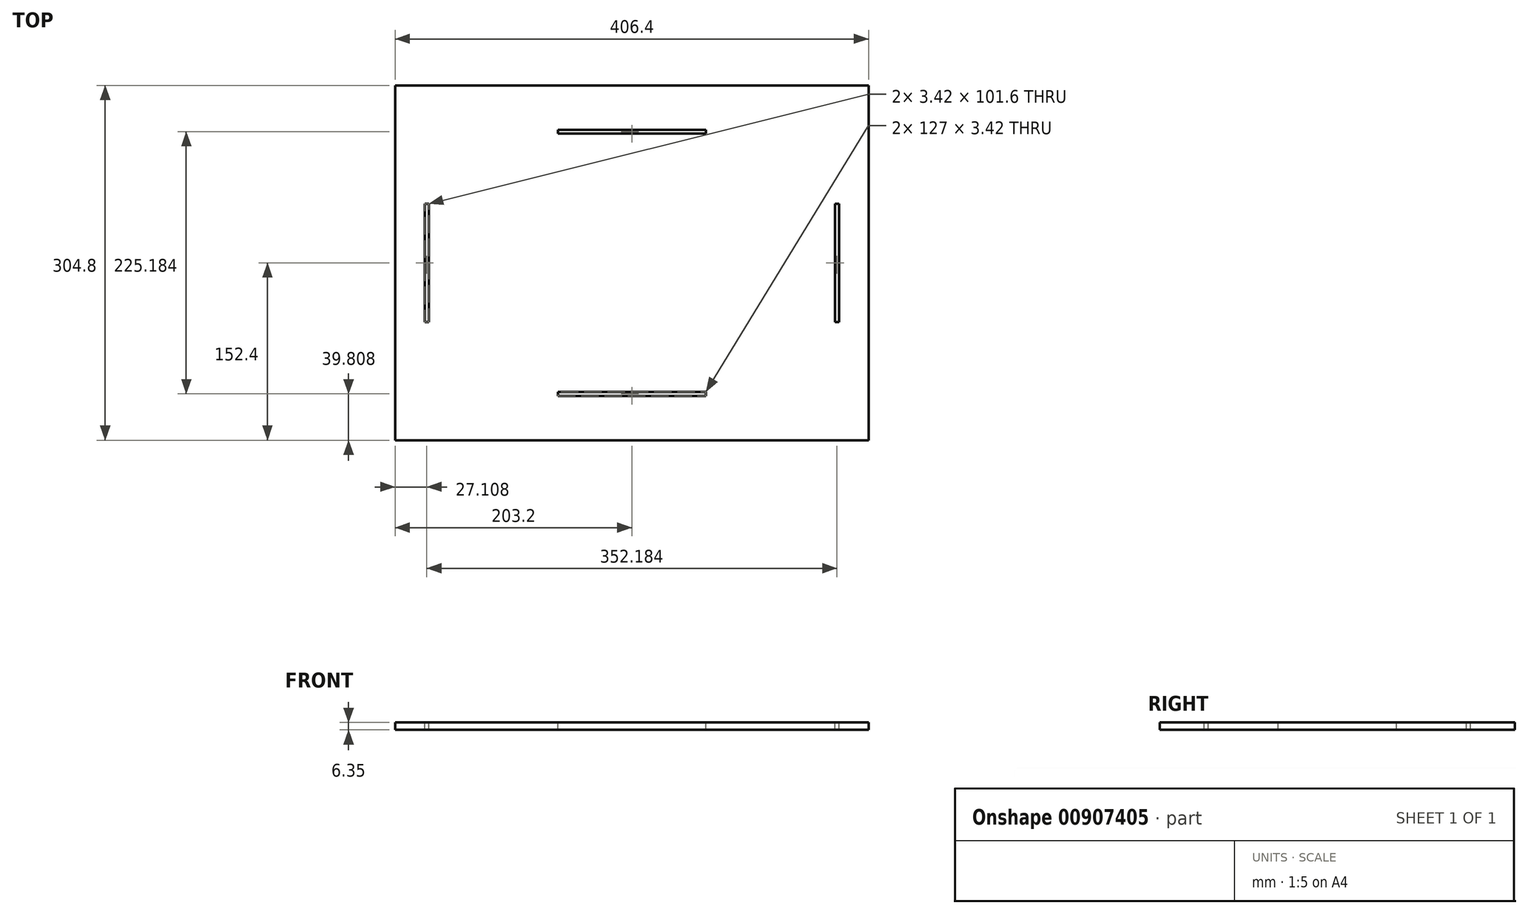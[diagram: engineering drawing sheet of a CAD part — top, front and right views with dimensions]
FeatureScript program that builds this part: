
annotation { "Feature Type Name" : "Feature", "Feature Type Description" : "" }
export const myFeature = defineFeature(function(context is Context, id is Id, definition is map)
    precondition{}
    {
        {
            var Q0;
            Q0=qCreatedBy(makeId("Top.planeOp"),FACE);
            var sketch = newSketch(context, id + "F0", { "sketchPlane" : qUnion([Q0])});
            skLineSegment(sketch, "E0.bottom", {"start": v(-203.2, 152.4) * mm, "end": v(203.2, 152.4) * mm});
            skLineSegment(sketch, "E0.top", {"start": v(-203.2, -152.4) * mm, "end": v(203.2, -152.4) * mm});
            skLineSegment(sketch, "E0.left", {"start": v(-203.2, 152.4) * mm, "end": v(-203.2, -152.4) * mm});
            skLineSegment(sketch, "E0.right", {"start": v(203.2, 152.4) * mm, "end": v(203.2, -152.4) * mm});
            skLineSegment(sketch, "E1.bottom", {"start": v(-177.8, 50.8) * mm, "end": v(-174.38, 50.8) * mm});
            skLineSegment(sketch, "E1.top", {"start": v(-177.8, -50.8) * mm, "end": v(-174.38, -50.8) * mm});
            skLineSegment(sketch, "E1.left", {"start": v(-177.8, 50.8) * mm, "end": v(-177.8, -50.8) * mm});
            skLineSegment(sketch, "E1.right", {"start": v(-174.38, 50.8) * mm, "end": v(-174.38, -50.8) * mm});
            skLineSegment(sketch, "E2.bottom", {"start": v(-63.5, 114.3) * mm, "end": v(63.5, 114.3) * mm});
            skLineSegment(sketch, "E2.top", {"start": v(-63.5, 110.88) * mm, "end": v(63.5, 110.88) * mm});
            skLineSegment(sketch, "E2.left", {"start": v(-63.5, 114.3) * mm, "end": v(-63.5, 110.88) * mm});
            skLineSegment(sketch, "E2.right", {"start": v(63.5, 114.3) * mm, "end": v(63.5, 110.88) * mm});
            skLineSegment(sketch, "E3.bottom", {"start": v(-63.5, -110.88) * mm, "end": v(63.5, -110.88) * mm});
            skLineSegment(sketch, "E3.top", {"start": v(-63.5, -114.3) * mm, "end": v(63.5, -114.3) * mm});
            skLineSegment(sketch, "E3.left", {"start": v(-63.5, -110.88) * mm, "end": v(-63.5, -114.3) * mm});
            skLineSegment(sketch, "E3.right", {"start": v(63.5, -110.88) * mm, "end": v(63.5, -114.3) * mm});
            skLineSegment(sketch, "E4.bottom", {"start": v(174.38, 50.8) * mm, "end": v(177.8, 50.8) * mm});
            skLineSegment(sketch, "E4.top", {"start": v(174.38, -50.8) * mm, "end": v(177.8, -50.8) * mm});
            skLineSegment(sketch, "E4.left", {"start": v(174.38, 50.8) * mm, "end": v(174.38, -50.8) * mm});
            skLineSegment(sketch, "E4.right", {"start": v(177.8, 50.8) * mm, "end": v(177.8, -50.8) * mm});
            skLineSegment(sketch, "E5", {"start": v(-177.8, 50.8) * mm, "end": v(-177.8, 114.3) * mm, "construction": true});
            skLineSegment(sketch, "E6", {"start": v(-177.8, 114.3) * mm, "end": v(-63.5, 114.3) * mm, "construction": true});
            skLineSegment(sketch, "E7", {"start": v(63.5, 114.3) * mm, "end": v(177.8, 114.3) * mm, "construction": true});
            skLineSegment(sketch, "E8", {"start": v(177.8, 114.3) * mm, "end": v(177.8, 50.8) * mm, "construction": true});
            skLineSegment(sketch, "E9", {"start": v(177.8, -50.8) * mm, "end": v(177.8, -114.3) * mm, "construction": true});
            skLineSegment(sketch, "E10", {"start": v(177.8, -114.3) * mm, "end": v(63.5, -114.3) * mm, "construction": true});
            skLineSegment(sketch, "E11", {"start": v(-63.5, -114.3) * mm, "end": v(-177.8, -114.3) * mm, "construction": true});
            skLineSegment(sketch, "E12", {"start": v(-177.8, -114.3) * mm, "end": v(-177.8, -50.8) * mm, "construction": true});
            skSolve(sketch);
        }
        {
            var Q0;
            Q0=makeQuery(id+"F0.imprint","IMPRINT",FACE,{"disambiguationData":[TD([[makeQuery(id+"F0.imprint","IMPRINT",EDGE,{"derivedFrom":sQuery(id+"F0.wireOp",EDGE,"E0.bottom")}),-1.0]])]});
            extrude(context, id + "F1", {"entities" : qUnion([Q0]), "oppositeDirection" : true, "depth" : 6.35 * mm, "offsetDistance" : 25.4 * mm});
        }
    });
